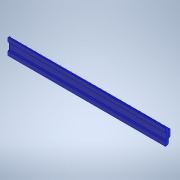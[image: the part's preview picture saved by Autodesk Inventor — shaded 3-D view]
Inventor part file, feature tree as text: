
AUTODESK INVENTOR PART (.ipt)
format: ipt  version: 2020.3 (Build 243373000, 373)  size: 295,424 bytes
history: native  units: mm (DEFAULTED — no unit token found)
features: extrude x2, sketch x2, pattern_linear x1
ambient origin geometry x8: Origin, YZ Plane, XZ Plane, XY Plane, X Axis, Y Axis, Z Axis, Center Point
bodies: Solid1 (feature_tree)
feature tree (5):
  extrude  "Extrusion1"  Depth=5.0mm TaperAngle=0.0deg
  extrude  "Extrusion2"  [1 undecoded]
  pattern_linear  "Rectangular Pattern1"  [2 undecoded]
  sketch  "Sketch_1"  dims[d0=200.0mm d1=0.0mm d2=5.0mm d3=0.0mm]
  sketch  "Sketch_5"  dims[d4=6410.0mm d6=3.14159mm d7=10.0mm d9=0.0mm]
note: 3 required parameter values undecoded (feature->parameter linkage not recoverable at this tier; creation-order binding heuristic only, values carry confidence <= 0.55)
